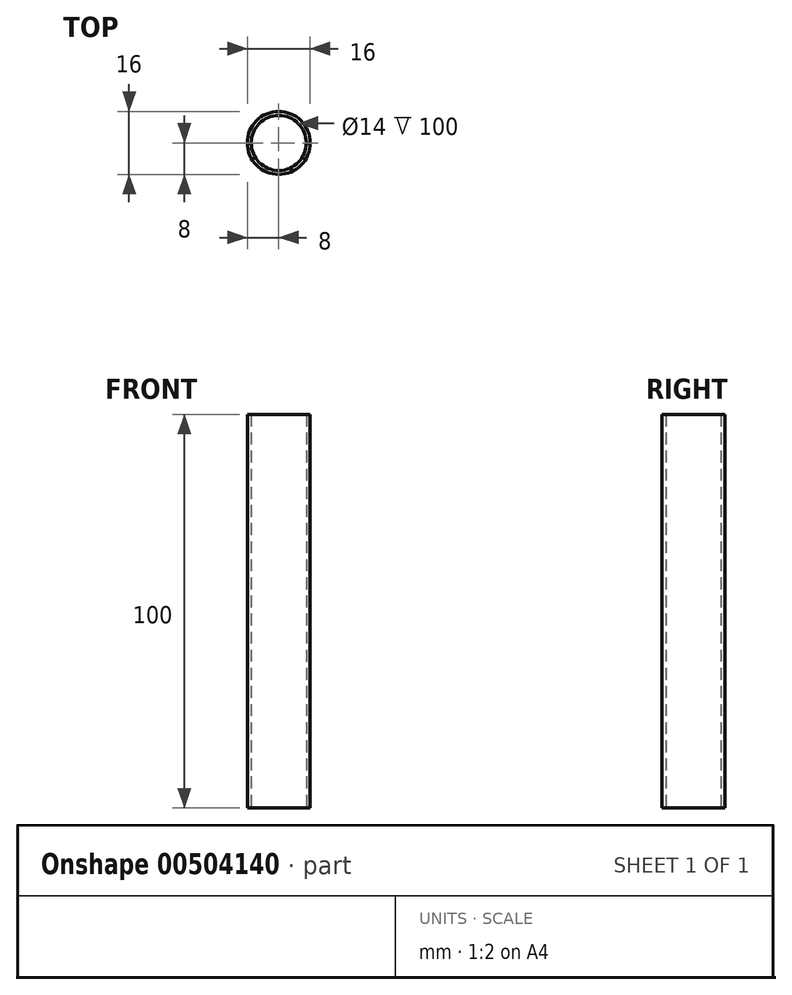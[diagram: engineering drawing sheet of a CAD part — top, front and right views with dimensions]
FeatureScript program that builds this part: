
annotation { "Feature Type Name" : "Feature", "Feature Type Description" : "" }
export const myFeature = defineFeature(function(context is Context, id is Id, definition is map)
    precondition{}
    {
        {
            var Q0;
            Q0=qCreatedBy(makeId("Top.planeOp"),FACE);
            var sketch = newSketch(context, id + "F0", { "sketchPlane" : qUnion([Q0])});
            skCircle(sketch, "E0", {"center": v(0, 0) * mm, "radius": 7 * mm});
            skCircle(sketch, "E1", {"center": v(0, 0) * mm, "radius": 8 * mm});
            skSolve(sketch);
        }
        {
            var Q0;
            Q0 = qSketchRegion(id + "F0", true);
            extrude(context, id + "F1", {"entities" : qUnion([Q0]), "depth" : 100 * mm, "offsetDistance" : 25 * mm});
        }
    });
